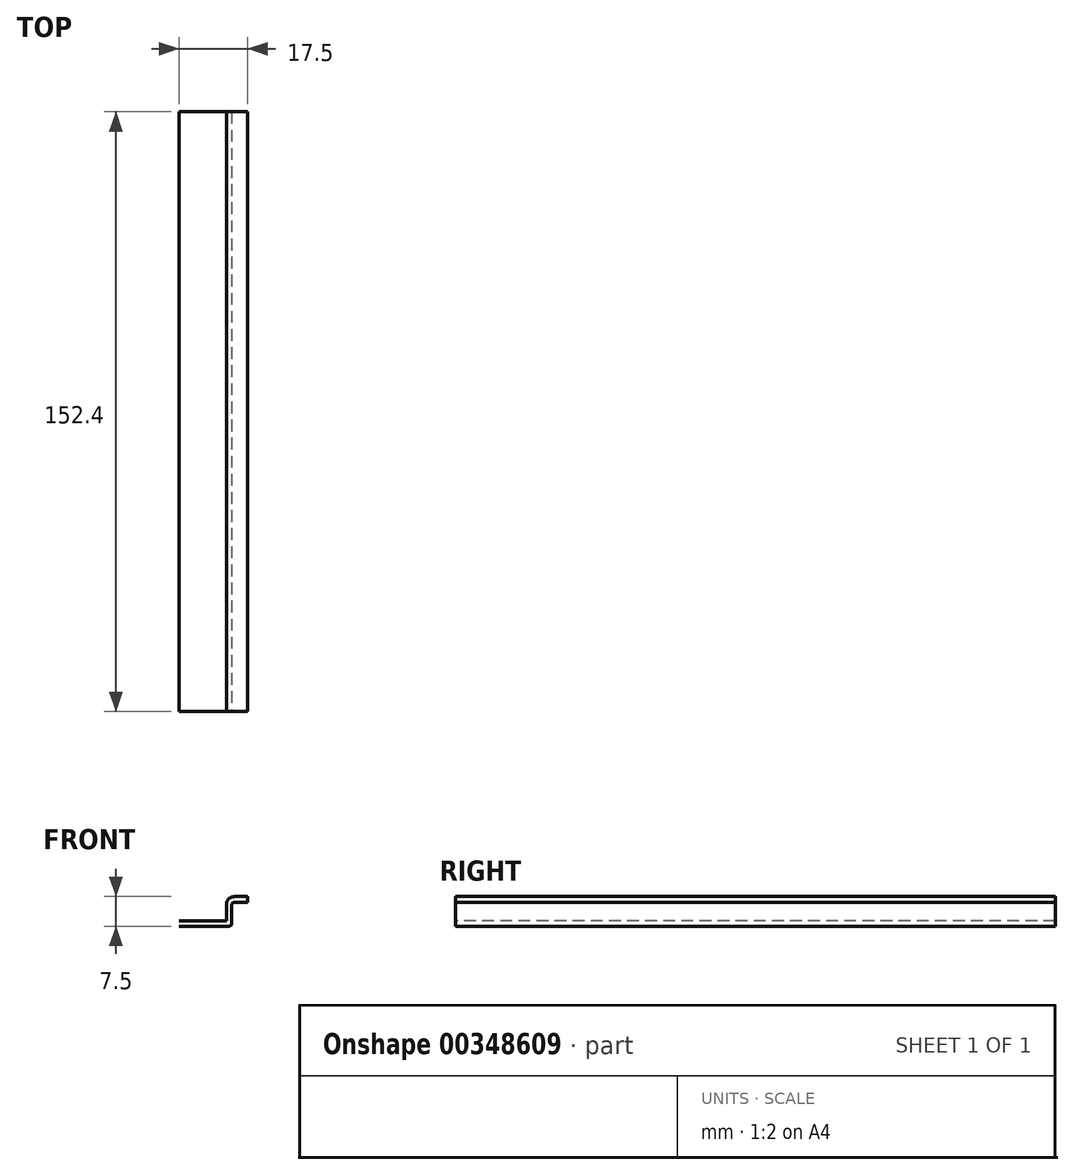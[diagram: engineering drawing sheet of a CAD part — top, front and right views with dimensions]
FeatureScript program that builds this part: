
annotation { "Feature Type Name" : "Feature", "Feature Type Description" : "" }
export const myFeature = defineFeature(function(context is Context, id is Id, definition is map)
    precondition{}
    {
        {
            var Q0;
            Q0=qCreatedBy(makeId("Front.planeOp"),FACE);
            var sketch = newSketch(context, id + "F0", { "sketchPlane" : qUnion([Q0])});
            skLineSegment(sketch, "E0", {"start": v(0, 0) * mm, "end": v(12.8, 0) * mm});
            skLineSegment(sketch, "E1", {"start": v(13.45, 0.65) * mm, "end": v(13.45, 5.45) * mm});
            skLineSegment(sketch, "E2", {"start": v(14.1, 6.1) * mm, "end": v(17.5, 6.1) * mm});
            skPoint(sketch, "E3.visualSharp", {"position": v(13.45, 0) * mm});
            skArc(sketch, "E3.filletArc", {"start": v(12.8, 0) * mm, "mid": v(13.26, 0.19) * mm, "end": v(13.45, 0.65) * mm});
            skPoint(sketch, "E4.visualSharp", {"position": v(13.45, 6.1) * mm});
            skArc(sketch, "E4.filletArc", {"start": v(14.1, 6.1) * mm, "mid": v(13.64, 5.91) * mm, "end": v(13.45, 5.45) * mm});
            skLineSegment(sketch, "E5.0", {"start": v(14.1, 7.5) * mm, "end": v(17.5, 7.5) * mm});
            skArc(sketch, "E5.1", {"start": v(14.1, 7.5) * mm, "mid": v(12.65, 6.9) * mm, "end": v(12.05, 5.45) * mm});
            skLineSegment(sketch, "E5.2", {"start": v(12.05, 1.4) * mm, "end": v(12.05, 5.45) * mm});
            skLineSegment(sketch, "E5.3", {"start": v(0, 1.4) * mm, "end": v(12.05, 1.4) * mm});
            skLineSegment(sketch, "E6", {"start": v(17.5, 7.5) * mm, "end": v(17.5, 6.1) * mm});
            skSolve(sketch);
        }
        {
            var Q0;
            Q0=sQuery(id+"FsiOYvrTF1NMHw2_0.1.F0.wireOp",EDGE,"E0");
            var Q1;
            Q1=sQuery(id+"F0.wireOp",EDGE,"E0");
            var Q2;
            Q2=sQuery(id+"F0.wireOp",EDGE,"E5.3");
            var Q3;
            Q3=sQuery(id+"FsiOYvrTF1NMHw2_0.1.F0.wireOp",EDGE,"E5.3");
            var Q4;
            Q4=sQuery(id+"F0.wireOp",EDGE,"E6");
            var Q5;
            Q5=sQuery(id+"FsiOYvrTF1NMHw2_0.1.F0.wireOp",EDGE,"E6");
            var Q6;
            Q6=sQuery(id+"F0.wireOp",EDGE,"E5.0");
            var Q7;
            Q7=sQuery(id+"F0.wireOp",EDGE,"E2");
            var Q8;
            Q8=sQuery(id+"FsiOYvrTF1NMHw2_0.1.F0.wireOp",EDGE,"E1");
            var Q9;
            Q9=sQuery(id+"FsiOYvrTF1NMHw2_0.1.F0.wireOp",EDGE,"E2");
            var Q10;
            Q10=sQuery(id+"FsiOYvrTF1NMHw2_0.1.F0.wireOp",EDGE,"E4.filletArc");
            var Q11;
            Q11=sQuery(id+"FsiOYvrTF1NMHw2_0.1.F0.wireOp",EDGE,"E5.0");
            var Q12;
            Q12=sQuery(id+"FsiOYvrTF1NMHw2_0.1.F0.wireOp",EDGE,"E5.1");
            var Q13;
            Q13=sQuery(id+"FsiOYvrTF1NMHw2_0.1.F0.wireOp",EDGE,"E5.2");
            var Q14;
            Q14=sQuery(id+"F0.wireOp",EDGE,"E3.filletArc");
            var Q15;
            Q15=sQuery(id+"F0.wireOp",EDGE,"E1");
            var Q16;
            Q16=sQuery(id+"F0.wireOp",EDGE,"E5.2");
            var Q17;
            Q17=sQuery(id+"F0.wireOp",EDGE,"E5.1");
            var Q18;
            Q18=sQuery(id+"F0.wireOp",EDGE,"E4.filletArc");
            var Q19;
            Q19=sQuery(id+"FsiOYvrTF1NMHw2_0.1.F0.wireOp",EDGE,"E3.filletArc");
            extrude(context, id + "F1", {"bodyType" : ToolBodyType.SURFACE, "surfaceEntities" : qUnion([Q0, Q1, Q2, Q3, Q4, Q5, Q6, Q7, Q8, Q9, Q10, Q11, Q12, Q13, Q14, Q15, Q16, Q17, Q18, Q19]), "depth" : 152.4 * mm});
        }
    });
